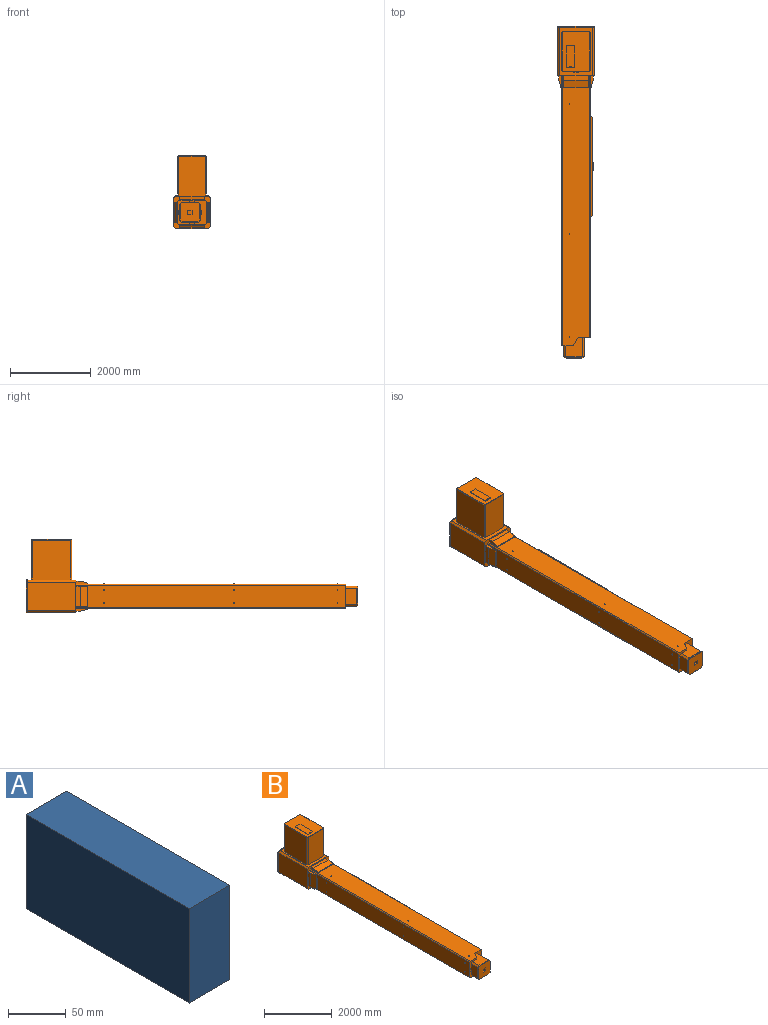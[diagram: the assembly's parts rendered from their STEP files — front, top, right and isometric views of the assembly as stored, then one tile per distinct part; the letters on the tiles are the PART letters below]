
ASSEMBLY  parts=2 mates=1
PART A: 6 faces, bbox 50x200x100 mm
  f0: plane 200x50mm, normal (0,0,1), area 10000mm2, adj f1,f3,f4,f5
  f1: plane 100x50mm, normal (0,-1,0), area 5000mm2, adj f0,f2,f4,f5
  f2: plane 200x50mm, normal (0,0,-1), area 10000mm2, adj f1,f3,f4,f5
  f3: plane 100x50mm, normal (0,1,0), area 5000mm2, adj f0,f2,f4,f5
  f4: plane 200x100mm, normal (1,0,0), area 20000mm2, adj f0,f1,f2,f3
  f5: plane 200x100mm, normal (-1,0,0), area 20000mm2, adj f0,f1,f2,f3
PART B: 257 faces, bbox 920x8235x1820 mm
  f0: plane 2450x500mm, normal (1,0,0), area 1205000mm2, adj f25,f27,f29,f30,f252,f253,f254,f255
  f1: plane 1200x800mm, normal (0,0,1), area 257250mm2, adj f34,f36,f38,f155,f156,f157,f158,f159
  f2: plane 550x200mm, normal (0,0,1), area 109300mm2, adj f219,f220,f221,f222,f223,f224,f225,f226
  f3: plane 980x680mm, normal (0,0,1), area 555867.2mm2, adj f219,f220,f221,f222,f223,f224,f225,f226
  f4: plane 475x400mm, normal (0,0,-1), area 141547mm2, adj f9,f10,f16,f17,f19,f196
  f5: plane 500x400mm, normal (1,0,0), area 192500mm2, adj f10,f19,f20,f59,f60,f63,f196
  f6: plane 475x400mm, normal (0,0,1), area 141547mm2, adj f9,f10,f14,f18,f20,f196
  f7: plane 400x300mm, normal (-1,0,0), area 112500mm2, adj f9,f17,f18,f61,f62,f64,f196
  f8: plane 920x820mm, normal (0,1,0), area 746559.8mm2, adj f160,f161,f162,f163,f164,f165,f166,f167
  f9: plane 600x284.53mm, normal (0,-1,0), area 52828mm2, adj f4,f6,f7,f11,f12,f14,f15,f16
  f10: plane 600x300mm, normal (0,-1,0), area 104375mm2, adj f4,f5,f6,f12,f13,f14,f15,f16
  f11: plane 6700x550mm, normal (-1,0,0), area 3532600mm2, adj f9,f21,f23,f34,f51,f52,f54,f125
  f12: plane 6700x650mm, normal (0,0,1), area 4107253mm2, adj f9,f10,f14,f23,f24,f34,f39,f40
  f13: plane 6500x550mm, normal (1,0,0), area 2172600mm2, adj f10,f22,f24,f25,f26,f27,f28,f34
  f14: plane 200x115.47mm, normal (0.87,-0.5,0), area 11547mm2, adj f6,f9,f10,f12
  f15: plane 6700x650mm, normal (0,0,-1), area 4107253mm2, adj f9,f10,f16,f21,f22,f34,f47,f48
  f16: plane 200x115.47mm, normal (0.87,-0.5,0), area 11547mm2, adj f4,f9,f10,f15
  f17: plane 275x50mm, normal (-0.71,0,-0.71), area 19445.4mm2, adj f4,f7,f9,f196
  f18: plane 275x50mm, normal (-0.71,0,0.71), area 19445.4mm2, adj f6,f7,f9,f196
  f19: plane 475x50mm, normal (0.71,0,-0.71), area 33587.6mm2, adj f4,f5,f10,f196
  f20: plane 475x50mm, normal (0.71,0,0.71), area 33587.6mm2, adj f5,f6,f10,f196
  f21: plane 6700x25mm, normal (-0.71,0,-0.71), area 236880.8mm2, adj f9,f11,f15,f34
  f22: plane 6500x25mm, normal (0.71,0,-0.71), area 229809.7mm2, adj f10,f13,f15,f34
  f23: plane 6700x25mm, normal (-0.71,0,0.71), area 236880.8mm2, adj f9,f11,f12,f34
  f24: plane 6500x25mm, normal (0.71,0,0.71), area 229809.7mm2, adj f10,f12,f13,f34
  f25: plane 2500x50mm, normal (0,0,1), area 124375mm2, adj f0,f13,f26,f28,f29,f30
  f26: plane 500x25mm, normal (0,-1,0), area 12500mm2, adj f13,f25,f27,f30
  f27: plane 2500x50mm, normal (0,0,-1), area 124375mm2, adj f0,f13,f26,f28,f29,f30
  f28: plane 500x25mm, normal (0,1,0), area 12500mm2, adj f13,f25,f27,f29
  f29: plane 500x25mm, normal (0.71,0.71,0), area 17677.7mm2, adj f0,f25,f27,f28
  f30: plane 500x25mm, normal (0.71,-0.71,0), area 17677.7mm2, adj f0,f25,f26,f27
  f31: plane 1200x700mm, normal (1,0,0), area 840000mm2, adj f34,f37,f38,f159
  f32: plane 1200x800mm, normal (0,0,-1), area 960000mm2, adj f34,f35,f37,f159
  f33: plane 1200x700mm, normal (-1,0,0), area 840000mm2, adj f34,f35,f36,f159
  f34: plane 900x800mm, normal (0,-1,0), area 131250mm2, adj f1,f11,f12,f13,f15,f21,f22,f23
  f35: plane 1200x50mm, normal (-0.71,0,-0.71), area 84852.8mm2, adj f32,f33,f34,f159
  f36: plane 1200x50mm, normal (-0.71,0,0.71), area 84852.8mm2, adj f1,f33,f34,f159
  f37: plane 1200x50mm, normal (0.71,0,-0.71), area 84852.8mm2, adj f31,f32,f34,f159
  f38: plane 1200x50mm, normal (0.71,0,0.71), area 84852.8mm2, adj f1,f31,f34,f159
  f39: plane 300x75mm, normal (-1,0,0), area 17834.9mm2, adj f12,f34,f41,f42,f58
  f40: plane 300x75mm, normal (1,0,0), area 17834.9mm2, adj f12,f34,f41,f42,f58
  f41: plane 600x113.4mm, normal (0,0,1), area 68038.5mm2, adj f34,f39,f40,f58
  f42: plane 600x25mm, normal (0,-1,0), area 15000mm2, adj f12,f39,f40,f58
  f43: plane 300x75mm, normal (0,0,1), area 17834.9mm2, adj f13,f34,f45,f46,f57
  f44: plane 300x75mm, normal (0,0,-1), area 17834.9mm2, adj f13,f34,f45,f46,f57
  f45: plane 500x113.4mm, normal (1,0,0), area 56698.7mm2, adj f34,f43,f44,f57
  f46: plane 500x25mm, normal (0,-1,0), area 12500mm2, adj f13,f43,f44,f57
  f47: plane 300x75mm, normal (1,0,0), area 17834.9mm2, adj f15,f34,f49,f50,f56
  f48: plane 300x75mm, normal (-1,0,0), area 17834.9mm2, adj f15,f34,f49,f50,f56
  f49: plane 600x113.4mm, normal (0,0,-1), area 68038.5mm2, adj f34,f47,f48,f56
  f50: plane 600x25mm, normal (0,-1,0), area 15000mm2, adj f15,f47,f48,f56
  f51: plane 300x75mm, normal (0,0,-1), area 17834.9mm2, adj f11,f34,f53,f54,f55
  f52: plane 300x75mm, normal (0,0,1), area 17834.9mm2, adj f11,f34,f53,f54,f55
  f53: plane 500x113.4mm, normal (-1,0,0), area 56698.7mm2, adj f34,f51,f52,f55
  f54: plane 500x25mm, normal (0,-1,0), area 12500mm2, adj f11,f51,f52,f55
  f55: plane 500x186.6mm, normal (-0.97,-0.26,0), area 96592.6mm2, adj f51,f52,f53,f54
  f56: plane 600x186.6mm, normal (0,-0.26,-0.97), area 115911.1mm2, adj f47,f48,f49,f50
  f57: plane 500x186.6mm, normal (0.97,-0.26,0), area 96592.6mm2, adj f43,f44,f45,f46
  f58: plane 600x186.6mm, normal (0,-0.26,0.97), area 115911.1mm2, adj f39,f40,f41,f42
  f59: plane 25x25mm, normal (0,0,-1), area 312.5mm2, adj f5,f10,f63
  f60: plane 25x25mm, normal (0,0,1), area 312.5mm2, adj f5,f10,f63
  f61: plane 25x25mm, normal (0,0,-1), area 312.5mm2, adj f7,f9,f64
  f62: plane 25x25mm, normal (0,0,1), area 312.5mm2, adj f7,f9,f64
  f63: plane 100x25mm, normal (-0.71,-0.71,0), area 3535.5mm2, adj f5,f10,f59,f60
  f64: plane 100x25mm, normal (0.71,-0.71,0), area 3535.5mm2, adj f7,f9,f61,f62
  f65: plane 20x10mm, normal (0,0,1), area 200mm2, adj f13,f66,f68,f69
  f66: plane 20x10mm, normal (0,-1,0), area 200mm2, adj f13,f65,f67,f69
  f67: plane 20x10mm, normal (0,0,-1), area 200mm2, adj f13,f66,f68,f69
  f68: plane 20x10mm, normal (0,1,0), area 200mm2, adj f13,f65,f67,f69
  f69: plane 20x20mm, normal (1,0,0), area 400mm2, adj f65,f66,f67,f68
  f70: plane 20x10mm, normal (0,0,1), area 200mm2, adj f13,f71,f73,f74
  f71: plane 20x10mm, normal (0,-1,0), area 200mm2, adj f13,f70,f72,f74
  f72: plane 20x10mm, normal (0,0,-1), area 200mm2, adj f13,f71,f73,f74
  f73: plane 20x10mm, normal (0,1,0), area 200mm2, adj f13,f70,f72,f74
  f74: plane 20x20mm, normal (1,0,0), area 400mm2, adj f70,f71,f72,f73
  f75: plane 20x10mm, normal (0,-1,0), area 200mm2, adj f13,f76,f78,f79
  f76: plane 20x10mm, normal (0,0,-1), area 200mm2, adj f13,f75,f77,f79
  f77: plane 20x10mm, normal (0,1,0), area 200mm2, adj f13,f76,f78,f79
  f78: plane 20x10mm, normal (0,0,1), area 200mm2, adj f13,f75,f77,f79
  f79: plane 20x20mm, normal (1,0,0), area 400mm2, adj f75,f76,f77,f78
  f80: plane 20x10mm, normal (0,-1,0), area 200mm2, adj f13,f81,f83,f84
  f81: plane 20x10mm, normal (0,0,-1), area 200mm2, adj f13,f80,f82,f84
  f82: plane 20x10mm, normal (0,1,0), area 200mm2, adj f13,f81,f83,f84
  f83: plane 20x10mm, normal (0,0,1), area 200mm2, adj f13,f80,f82,f84
  f84: plane 20x20mm, normal (1,0,0), area 400mm2, adj f80,f81,f82,f83
  f85: plane 20x10mm, normal (0,0,1), area 200mm2, adj f13,f86,f88,f89
  f86: plane 20x10mm, normal (0,-1,0), area 200mm2, adj f13,f85,f87,f89
  f87: plane 20x10mm, normal (0,0,-1), area 200mm2, adj f13,f86,f88,f89
  f88: plane 20x10mm, normal (0,1,0), area 200mm2, adj f13,f85,f87,f89
  f89: plane 20x20mm, normal (1,0,0), area 400mm2, adj f85,f86,f87,f88
  f90: plane 20x10mm, normal (0,0,1), area 200mm2, adj f13,f91,f93,f94
  f91: plane 20x10mm, normal (0,-1,0), area 200mm2, adj f13,f90,f92,f94
  f92: plane 20x10mm, normal (0,0,-1), area 200mm2, adj f13,f91,f93,f94
  f93: plane 20x10mm, normal (0,1,0), area 200mm2, adj f13,f90,f92,f94
  f94: plane 20x20mm, normal (1,0,0), area 400mm2, adj f90,f91,f92,f93
  f95: plane 20x10mm, normal (0,1,0), area 200mm2, adj f12,f96,f98,f99
  f96: plane 20x10mm, normal (-1,0,0), area 200mm2, adj f12,f95,f97,f99
  f97: plane 20x10mm, normal (0,-1,0), area 200mm2, adj f12,f96,f98,f99
  f98: plane 20x10mm, normal (1,0,0), area 200mm2, adj f12,f95,f97,f99
  f99: plane 20x20mm, normal (0,0,1), area 400mm2, adj f95,f96,f97,f98
  f100: plane 20x10mm, normal (0,-1,0), area 200mm2, adj f12,f101,f103,f104
  f101: plane 20x10mm, normal (1,0,0), area 200mm2, adj f12,f100,f102,f104
  f102: plane 20x10mm, normal (0,1,0), area 200mm2, adj f12,f101,f103,f104
  f103: plane 20x10mm, normal (-1,0,0), area 200mm2, adj f12,f100,f102,f104
  f104: plane 20x20mm, normal (0,0,1), area 400mm2, adj f100,f101,f102,f103
  f105: plane 20x10mm, normal (-1,0,0), area 200mm2, adj f12,f106,f108,f109
  f106: plane 20x10mm, normal (0,-1,0), area 200mm2, adj f12,f105,f107,f109
  f107: plane 20x10mm, normal (1,0,0), area 200mm2, adj f12,f106,f108,f109
  f108: plane 20x10mm, normal (0,1,0), area 200mm2, adj f12,f105,f107,f109
  f109: plane 20x20mm, normal (0,0,1), area 400mm2, adj f105,f106,f107,f108
  f110: plane 20x10mm, normal (0,-1,0), area 200mm2, adj f15,f111,f113,f114
  f111: plane 20x10mm, normal (-1,0,0), area 200mm2, adj f15,f110,f112,f114
  f112: plane 20x10mm, normal (0,1,0), area 200mm2, adj f15,f111,f113,f114
  f113: plane 20x10mm, normal (1,0,0), area 200mm2, adj f15,f110,f112,f114
  f114: plane 20x20mm, normal (0,0,-1), area 400mm2, adj f110,f111,f112,f113
  f115: plane 20x10mm, normal (0,-1,0), area 200mm2, adj f15,f116,f118,f119
  f116: plane 20x10mm, normal (-1,0,0), area 200mm2, adj f15,f115,f117,f119
  f117: plane 20x10mm, normal (0,1,0), area 200mm2, adj f15,f116,f118,f119
  f118: plane 20x10mm, normal (1,0,0), area 200mm2, adj f15,f115,f117,f119
  f119: plane 20x20mm, normal (0,0,-1), area 400mm2, adj f115,f116,f117,f118
  f120: plane 20x10mm, normal (0,-1,0), area 200mm2, adj f15,f121,f123,f124
  f121: plane 20x10mm, normal (-1,0,0), area 200mm2, adj f15,f120,f122,f124
  f122: plane 20x10mm, normal (0,1,0), area 200mm2, adj f15,f121,f123,f124
  f123: plane 20x10mm, normal (1,0,0), area 200mm2, adj f15,f120,f122,f124
  f124: plane 20x20mm, normal (0,0,-1), area 400mm2, adj f120,f121,f122,f123
  f125: plane 20x10mm, normal (0,0,1), area 200mm2, adj f11,f126,f128,f129
  f126: plane 20x10mm, normal (0,1,0), area 200mm2, adj f11,f125,f127,f129
  f127: plane 20x10mm, normal (0,0,-1), area 200mm2, adj f11,f126,f128,f129
  f128: plane 20x10mm, normal (0,-1,0), area 200mm2, adj f11,f125,f127,f129
  f129: plane 20x20mm, normal (-1,0,0), area 400mm2, adj f125,f126,f127,f128
  f130: plane 20x10mm, normal (0,0,1), area 200mm2, adj f11,f131,f133,f134
  f131: plane 20x10mm, normal (0,1,0), area 200mm2, adj f11,f130,f132,f134
  f132: plane 20x10mm, normal (0,0,-1), area 200mm2, adj f11,f131,f133,f134
  f133: plane 20x10mm, normal (0,-1,0), area 200mm2, adj f11,f130,f132,f134
  f134: plane 20x20mm, normal (-1,0,0), area 400mm2, adj f130,f131,f132,f133
  f135: plane 20x10mm, normal (0,-1,0), area 200mm2, adj f11,f136,f138,f139
  f136: plane 20x10mm, normal (0,0,1), area 200mm2, adj f11,f135,f137,f139
  f137: plane 20x10mm, normal (0,1,0), area 200mm2, adj f11,f136,f138,f139
  f138: plane 20x10mm, normal (0,0,-1), area 200mm2, adj f11,f135,f137,f139
  f139: plane 20x20mm, normal (-1,0,0), area 400mm2, adj f135,f136,f137,f138
  f140: plane 20x10mm, normal (0,-1,0), area 200mm2, adj f11,f141,f143,f144
  f141: plane 20x10mm, normal (0,0,1), area 200mm2, adj f11,f140,f142,f144
  f142: plane 20x10mm, normal (0,1,0), area 200mm2, adj f11,f141,f143,f144
  f143: plane 20x10mm, normal (0,0,-1), area 200mm2, adj f11,f140,f142,f144
  f144: plane 20x20mm, normal (-1,0,0), area 400mm2, adj f140,f141,f142,f143
  f145: plane 20x10mm, normal (0,-1,0), area 200mm2, adj f11,f146,f148,f149
  f146: plane 20x10mm, normal (0,0,1), area 200mm2, adj f11,f145,f147,f149
  f147: plane 20x10mm, normal (0,1,0), area 200mm2, adj f11,f146,f148,f149
  f148: plane 20x10mm, normal (0,0,-1), area 200mm2, adj f11,f145,f147,f149
  f149: plane 20x20mm, normal (-1,0,0), area 400mm2, adj f145,f146,f147,f148
  f150: plane 20x10mm, normal (0,-1,0), area 200mm2, adj f11,f151,f153,f154
  f151: plane 20x10mm, normal (0,0,1), area 200mm2, adj f11,f150,f152,f154
  f152: plane 20x10mm, normal (0,1,0), area 200mm2, adj f11,f151,f153,f154
  f153: plane 20x10mm, normal (0,0,-1), area 200mm2, adj f11,f150,f152,f154
  f154: plane 20x20mm, normal (-1,0,0), area 400mm2, adj f150,f151,f152,f153
  f155: plane 1000x950mm, normal (-1,0,0), area 941500mm2, adj f1,f215,f216,f238,f240,f241,f249
  f156: plane 1000x650mm, normal (0,-1,0), area 644500mm2, adj f1,f216,f217,f234,f246,f247,f251
  f157: plane 1000x950mm, normal (1,0,0), area 941500mm2, adj f1,f217,f218,f233,f242,f243,f248
  f158: plane 1000x650mm, normal (0,1,0), area 644500mm2, adj f1,f215,f218,f237,f244,f245,f250
  f159: plane 920x820mm, normal (0,-1,0), area 33159.8mm2, adj f1,f31,f32,f33,f35,f36,f37,f38
  f160: plane 808.28x25mm, normal (0,0,1), area 20207.1mm2, adj f8,f159,f161,f167
  f161: plane 55.86x55.86mm, normal (0.71,0,0.71), area 1974.9mm2, adj f8,f159,f160,f162
  f162: plane 708.28x25mm, normal (1,0,0), area 17707.1mm2, adj f8,f159,f161,f163
  f163: plane 55.86x55.86mm, normal (0.71,0,-0.71), area 1974.9mm2, adj f8,f159,f162,f164
  f164: plane 808.28x25mm, normal (0,0,-1), area 20207.1mm2, adj f8,f159,f163,f165
  f165: plane 55.86x55.86mm, normal (-0.71,0,-0.71), area 1974.9mm2, adj f8,f159,f164,f166
  f166: plane 708.28x25mm, normal (-1,0,0), area 17707.1mm2, adj f8,f159,f165,f167
  f167: plane 55.86x55.86mm, normal (-0.71,0,0.71), area 1974.9mm2, adj f8,f159,f160,f166
  f168: plane 20x10mm, normal (0,0,1), area 200mm2, adj f8,f169,f171,f172
  f169: plane 20x10mm, normal (1,0,0), area 200mm2, adj f8,f168,f170,f172
  f170: plane 20x10mm, normal (0,0,-1), area 200mm2, adj f8,f169,f171,f172
  f171: plane 20x10mm, normal (-1,0,0), area 200mm2, adj f8,f168,f170,f172
  f172: plane 20x20mm, normal (0,1,0), area 400mm2, adj f168,f169,f170,f171
  f173: plane 20x10mm, normal (1,0,0), area 200mm2, adj f8,f174,f176,f177
  f174: plane 20x10mm, normal (0,0,-1), area 200mm2, adj f8,f173,f175,f177
  f175: plane 20x10mm, normal (-1,0,0), area 200mm2, adj f8,f174,f176,f177
  f176: plane 20x10mm, normal (0,0,1), area 200mm2, adj f8,f173,f175,f177
  f177: plane 20x20mm, normal (0,1,0), area 400mm2, adj f173,f174,f175,f176
  f178: plane 20x10mm, normal (-1,0,0), area 200mm2, adj f8,f179,f181,f182
  f179: plane 20x10mm, normal (0,0,1), area 200mm2, adj f8,f178,f180,f182
  f180: plane 20x10mm, normal (1,0,0), area 200mm2, adj f8,f179,f181,f182
  f181: plane 20x10mm, normal (0,0,-1), area 200mm2, adj f8,f178,f180,f182
  f182: plane 20x20mm, normal (0,1,0), area 400mm2, adj f178,f179,f180,f181
  f183: plane 20x10mm, normal (0,0,1), area 200mm2, adj f8,f184,f186,f187
  f184: plane 20x10mm, normal (1,0,0), area 200mm2, adj f8,f183,f185,f187
  f185: plane 20x10mm, normal (0,0,-1), area 200mm2, adj f8,f184,f186,f187
  f186: plane 20x10mm, normal (-1,0,0), area 200mm2, adj f8,f183,f185,f187
  f187: plane 20x20mm, normal (0,1,0), area 400mm2, adj f183,f184,f185,f186
  f188: plane 44.14x44.14mm, normal (-0.71,0,0.71), area 1560.7mm2, adj f189,f195,f196,f202
  f189: plane 391.72x25mm, normal (0,0,1), area 8792.9mm2, adj f188,f190,f196,f202,f209,f210,f212
  f190: plane 44.14x44.14mm, normal (0.71,0,0.71), area 1560.7mm2, adj f189,f191,f196,f202
  f191: plane 391.72x25mm, normal (1,0,0), area 8792.9mm2, adj f190,f192,f196,f202,f207,f208,f211
  f192: plane 44.14x44.14mm, normal (0.71,0,-0.71), area 1560.7mm2, adj f191,f193,f196,f202
  f193: plane 391.72x25mm, normal (0,0,-1), area 8792.9mm2, adj f192,f194,f196,f202,f205,f206,f214
  f194: plane 44.14x44.14mm, normal (-0.71,0,-0.71), area 1560.7mm2, adj f193,f195,f196,f202
  f195: plane 391.72x25mm, normal (-1,0,0), area 8792.9mm2, adj f188,f194,f196,f202,f203,f204,f213
  f196: plane 500x500mm, normal (0,-1,0), area 22497.1mm2, adj f4,f5,f6,f7,f17,f18,f19,f20
  f197: plane 100x100mm, normal (0,-1,0), area 10000mm2, adj f198,f199,f200,f201
  f198: plane 500x100mm, normal (0,0,1), area 50000mm2, adj f197,f199,f201,f202
  f199: plane 500x100mm, normal (-1,0,0), area 50000mm2, adj f197,f198,f200,f202
  f200: plane 500x100mm, normal (0,0,-1), area 50000mm2, adj f197,f199,f201,f202
  f201: plane 500x100mm, normal (1,0,0), area 50000mm2, adj f197,f198,f200,f202
  f202: plane 480x480mm, normal (0,-1,0), area 216502.9mm2, adj f188,f189,f190,f191,f192,f193,f194,f195
  f203: plane 10x10mm, normal (0,0,1), area 50mm2, adj f195,f196,f213
  f204: plane 10x10mm, normal (0,0,-1), area 50mm2, adj f195,f196,f213
  f205: plane 10x10mm, normal (1,0,0), area 50mm2, adj f193,f196,f214
  f206: plane 10x10mm, normal (-1,0,0), area 50mm2, adj f193,f196,f214
  f207: plane 10x10mm, normal (0,0,-1), area 50mm2, adj f191,f196,f211
  f208: plane 10x10mm, normal (0,0,1), area 50mm2, adj f191,f196,f211
  f209: plane 10x10mm, normal (1,0,0), area 50mm2, adj f189,f196,f212
  f210: plane 10x10mm, normal (-1,0,0), area 50mm2, adj f189,f196,f212
  f211: plane 100x10mm, normal (0.71,0.71,0), area 1414.2mm2, adj f191,f196,f207,f208
  f212: plane 100x10mm, normal (0,0.71,0.71), area 1414.2mm2, adj f189,f196,f209,f210
  f213: plane 100x10mm, normal (-0.71,0.71,0), area 1414.2mm2, adj f195,f196,f203,f204
  f214: plane 100x10mm, normal (0,0.71,-0.71), area 1414.2mm2, adj f193,f196,f205,f206
  f215: plane 990x25mm, normal (-0.71,0.71,0), area 35001.8mm2, adj f1,f155,f158,f239
  f216: plane 990x25mm, normal (-0.71,-0.71,0), area 35001.8mm2, adj f1,f155,f156,f236
  f217: plane 990x25mm, normal (0.71,-0.71,0), area 35001.8mm2, adj f1,f156,f157,f232
  f218: plane 990x25mm, normal (0.71,0.71,0), area 35001.8mm2, adj f1,f157,f158,f235
  f219: plane 180x10mm, normal (0,1,0), area 1800mm2, adj f2,f3,f223,f226
  f220: plane 530x10mm, normal (-1,0,0), area 5300mm2, adj f2,f3,f225,f226
  f221: plane 180x10mm, normal (0,-1,0), area 1800mm2, adj f2,f3,f224,f225
  f222: plane 530x10mm, normal (1,0,0), area 5300mm2, adj f2,f3,f223,f224
  f223: plane 10x10mm, normal (0.71,0.71,0), area 141.4mm2, adj f2,f3,f219,f222
  f224: plane 10x10mm, normal (0.71,-0.71,0), area 141.4mm2, adj f2,f3,f221,f222
  f225: plane 10x10mm, normal (-0.71,-0.71,0), area 141.4mm2, adj f2,f3,f220,f221
  f226: plane 10x10mm, normal (-0.71,0.71,0), area 141.4mm2, adj f2,f3,f219,f220
  f227: plane 10x10mm, normal (1,0,0), area 100mm2, adj f2,f228,f230,f231
  f228: plane 50x10mm, normal (0,1,0), area 500mm2, adj f2,f227,f229,f231
  f229: plane 10x10mm, normal (-1,0,0), area 100mm2, adj f2,f228,f230,f231
  f230: plane 50x10mm, normal (0,-1,0), area 500mm2, adj f2,f227,f229,f231
  f231: plane 50x10mm, normal (0,0,1), area 500mm2, adj f227,f228,f229,f230
  f232: plane 29.14x29.14mm, normal (0.5,-0.5,0.71), area 441.4mm2, adj f3,f217,f233,f234
  f233: plane 950x10mm, normal (0.71,0,0.71), area 13376.5mm2, adj f3,f157,f232,f235
  f234: plane 650x10mm, normal (0,-0.71,0.71), area 9133.8mm2, adj f3,f156,f232,f236
  f235: plane 29.14x29.14mm, normal (0.5,0.5,0.71), area 441.4mm2, adj f3,f218,f233,f237
  f236: plane 29.14x29.14mm, normal (-0.5,-0.5,0.71), area 441.4mm2, adj f3,f216,f234,f238
  f237: plane 650x10mm, normal (0,0.71,0.71), area 9133.8mm2, adj f3,f158,f235,f239
  f238: plane 950x10mm, normal (-0.71,0,0.71), area 13376.5mm2, adj f3,f155,f236,f239
  f239: plane 29.14x29.14mm, normal (-0.5,0.5,0.71), area 441.4mm2, adj f3,f215,f237,f238
  f240: plane 10x10mm, normal (0,-1,0), area 50mm2, adj f1,f155,f249
  f241: plane 10x10mm, normal (0,1,0), area 50mm2, adj f1,f155,f249
  f242: plane 10x10mm, normal (0,-1,0), area 50mm2, adj f1,f157,f248
  f243: plane 10x10mm, normal (0,1,0), area 50mm2, adj f1,f157,f248
  f244: plane 10x10mm, normal (1,0,0), area 50mm2, adj f1,f158,f250
  f245: plane 10x10mm, normal (-1,0,0), area 50mm2, adj f1,f158,f250
  f246: plane 10x10mm, normal (1,0,0), area 50mm2, adj f1,f156,f251
  f247: plane 10x10mm, normal (-1,0,0), area 50mm2, adj f1,f156,f251
  f248: plane 100x10mm, normal (-0.71,0,0.71), area 1414.2mm2, adj f1,f157,f242,f243
  f249: plane 100x10mm, normal (0.71,0,0.71), area 1414.2mm2, adj f1,f155,f240,f241
  f250: plane 100x10mm, normal (0,-0.71,0.71), area 1414.2mm2, adj f1,f158,f244,f245
  f251: plane 100x10mm, normal (0,0.71,0.71), area 1414.2mm2, adj f1,f156,f246,f247
  f252: plane 200x25mm, normal (0,0,-1), area 5000mm2, adj f0,f253,f255,f256
  f253: plane 100x25mm, normal (0,1,0), area 2500mm2, adj f0,f252,f254,f256
  f254: plane 200x25mm, normal (0,0,1), area 5000mm2, adj f0,f253,f255,f256
  f255: plane 100x25mm, normal (0,-1,0), area 2500mm2, adj f0,f252,f254,f256
  f256: plane 200x100mm, normal (1,0,0), area 20000mm2, adj f252,f253,f254,f255
PLACE A t=(-758.06,-3617.5,76.38)mm
PLACE B t=(-758.06,-3617.5,76.38)mm
MATE fastened A.f5 <-> B.f256  axis (-1,0,0) through (-33.06,632.5,376.38)mm
